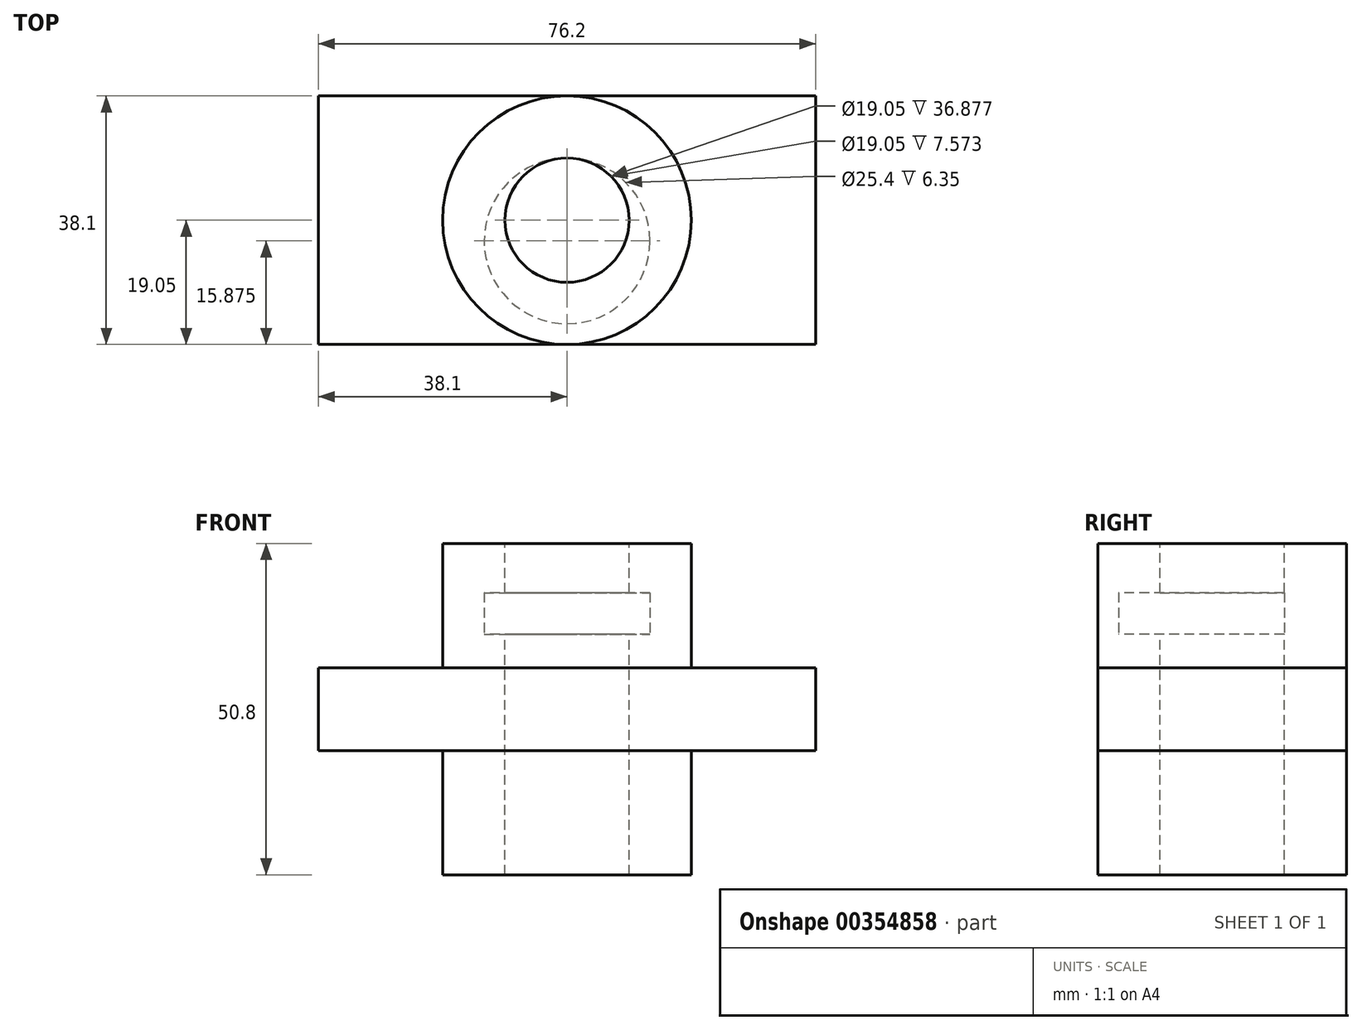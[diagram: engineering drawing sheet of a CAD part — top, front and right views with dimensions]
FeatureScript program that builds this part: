
annotation { "Feature Type Name" : "Feature", "Feature Type Description" : "" }
export const myFeature = defineFeature(function(context is Context, id is Id, definition is map)
    precondition{}
    {
        {
            var Q0;
            Q0=qCreatedBy(makeId("Top.planeOp"),FACE);
            var sketch = newSketch(context, id + "F0", { "sketchPlane" : qUnion([Q0])});
            skLineSegment(sketch, "E0.bottom", {"start": v(0, 0) * mm, "end": v(76.2, 0) * mm});
            skLineSegment(sketch, "E0.top", {"start": v(0, 38.1) * mm, "end": v(76.2, 38.1) * mm});
            skLineSegment(sketch, "E0.left", {"start": v(0, 0) * mm, "end": v(0, 38.1) * mm});
            skLineSegment(sketch, "E0.right", {"start": v(76.2, 0) * mm, "end": v(76.2, 38.1) * mm});
            skSolve(sketch);
        }
        {
            var Q0;
            Q0=makeQuery(id+"F0.imprint","IMPRINT",FACE,{"disambiguationData":[TD([[makeQuery(id+"F0.imprint","IMPRINT",EDGE,{"derivedFrom":sQuery(id+"F0.wireOp",EDGE,"E0.bottom")}),1.0]])]});
            extrude(context, id + "F1", {"entities" : qUnion([Q0]), "depth" : 12.7 * mm});
        }
        {
            var Q0;
            Q0=makeQuery(id+"F1.opExtrude","CAP_FACE",FACE,{"disambiguationData":[OSD([sQuery(id+"F0.wireOp",EDGE,"E0.bottom"),sQuery(id+"F0.wireOp",EDGE,"E0.top"),sQuery(id+"F0.wireOp",EDGE,"E0.left"),sQuery(id+"F0.wireOp",EDGE,"E0.right")])],"isStart":false});
            var sketch = newSketch(context, id + "F2", { "sketchPlane" : qUnion([Q0])});
            skCircle(sketch, "E1", {"center": v(38.1, 19.05) * mm, "radius": 19.05 * mm});
            skSolve(sketch);
        }
        {
            var Q0;
            {var subQ0=sQuery(id+"F2.wireOp",EDGE,"E1");var subQ1=makeQuery(id+"F2.imprint","INTERSECT",VERTEX,{"derivedFrom":[makeQuery(id+"F1.opExtrude","CAP_EDGE",EDGE,{"disambiguationData":[OSD([sQuery(id+"F0.wireOp",EDGE,"E0.bottom")])],"isStart":false}),subQ0]});Q0=makeQuery(id+"F2.imprint","IMPRINT",FACE,{"disambiguationData":[TD([[makeQuery(id+"F2.imprint","IMPRINT",EDGE,{"disambiguationData":[TD([[subQ1,1.0]])],"derivedFrom":subQ0}),1.0]])]});}
            extrude(context, id + "F3", {"entities" : qUnion([Q0]), "operationType" : NewBodyOperationType.ADD, "depth" : 19.05 * mm});
        }
        {
            var Q0;
            Q0=makeQuery(id+"F1.opExtrude","CAP_FACE",FACE,{"disambiguationData":[OSD([sQuery(id+"F0.wireOp",EDGE,"E0.bottom"),sQuery(id+"F0.wireOp",EDGE,"E0.top"),sQuery(id+"F0.wireOp",EDGE,"E0.left"),sQuery(id+"F0.wireOp",EDGE,"E0.right")])],"isStart":true});
            var sketch = newSketch(context, id + "F4", { "sketchPlane" : qUnion([Q0])});
            skCircle(sketch, "E2", {"center": v(38.1, -19.05) * mm, "radius": 19.05 * mm});
            skSolve(sketch);
        }
        {
            var Q0;
            {var subQ0=sQuery(id+"F4.wireOp",EDGE,"E2");var subQ1=makeQuery(id+"F4.imprint","INTERSECT",VERTEX,{"derivedFrom":[makeQuery(id+"F1.opExtrude","CAP_EDGE",EDGE,{"disambiguationData":[OSD([sQuery(id+"F0.wireOp",EDGE,"E0.bottom")])],"isStart":true}),subQ0]});Q0=makeQuery(id+"F4.imprint","IMPRINT",FACE,{"disambiguationData":[TD([[makeQuery(id+"F4.imprint","IMPRINT",EDGE,{"disambiguationData":[TD([[subQ1,-1.0]])],"derivedFrom":subQ0}),1.0]])]});}
            extrude(context, id + "F5", {"entities" : qUnion([Q0]), "operationType" : NewBodyOperationType.ADD, "depth" : 19.05 * mm});
        }
        {
            var Q0;
            Q0=qCreatedBy(makeId("Front.planeOp"),FACE);
            cPlane(context, id + "F6", {"entities" : qUnion([Q0]), "cplaneType" : CPlaneType.OFFSET, "offset" : 15.88 * mm, "oppositeDirection" : true, "width" : 152.4 * mm, "height" : 152.4 * mm});
        }
        {
            var Q0;
            Q0=makeQuery(id+"F3.opExtrude","CAP_FACE",FACE,{"disambiguationData":[OSD([sQuery(id+"F2.wireOp",EDGE,"E1")])],"isStart":false});
            var sketch = newSketch(context, id + "F7", { "sketchPlane" : qUnion([Q0])});
            skCircle(sketch, "E3", {"center": v(38.1, 19.05) * mm, "radius": 9.53 * mm});
            skSolve(sketch);
        }
        {
            var Q0;
            Q0=makeQuery(id+"F7.imprint","IMPRINT",FACE,{"disambiguationData":[TD([[makeQuery(id+"F7.imprint","IMPRINT",EDGE,{"derivedFrom":sQuery(id+"F7.wireOp",EDGE,"E3")}),1.0]])]});
            extrude(context, id + "F8", {"entities" : qUnion([Q0]), "operationType" : NewBodyOperationType.REMOVE, "endBound" : BoundingType.THROUGH_ALL, "oppositeDirection" : true, "depth" : 25.4 * mm});
        }
        {
            var Q0;
            Q0=qCreatedBy(id+"F6.planeOp",FACE);
            var sketch = newSketch(context, id + "F9", { "sketchPlane" : qUnion([Q0])});
            skLineSegment(sketch, "E4", {"start": v(38.1, 24.18) * mm, "end": v(38.1, 14.37) * mm});
            skLineSegment(sketch, "E5", {"start": v(50.8, 24.18) * mm, "end": v(38.1, 24.18) * mm});
            skLineSegment(sketch, "E6", {"start": v(50.8, 17.83) * mm, "end": v(38.1, 17.83) * mm});
            skLineSegment(sketch, "E7", {"start": v(50.8, 24.18) * mm, "end": v(50.8, 17.83) * mm});
            skLineSegment(sketch, "E8", {"start": v(57.15, 31.75) * mm, "end": v(57.15, 12.7) * mm});
            skSolve(sketch);
        }
        {
            var Q0;
            {var subQ0=sQuery(id+"F9.wireOp",EDGE,"E5");Q0=makeQuery(id+"F9.imprint","IMPRINT",FACE,{"disambiguationData":[TD([[makeQuery(id+"F9.imprint","IMPRINT",EDGE,{"derivedFrom":subQ0}),1.0]])]});}
            var Q1;
            Q1=sQuery(id+"F9.wireOp",EDGE,"E4");
            revolve(context, id + "F10", {"operationType" : NewBodyOperationType.REMOVE, "entities" : qUnion([Q0]), "axis" : qUnion([Q1]), "revolveType" : RevolveType.FULL, "oppositeDirection" : true});
        }
    });
